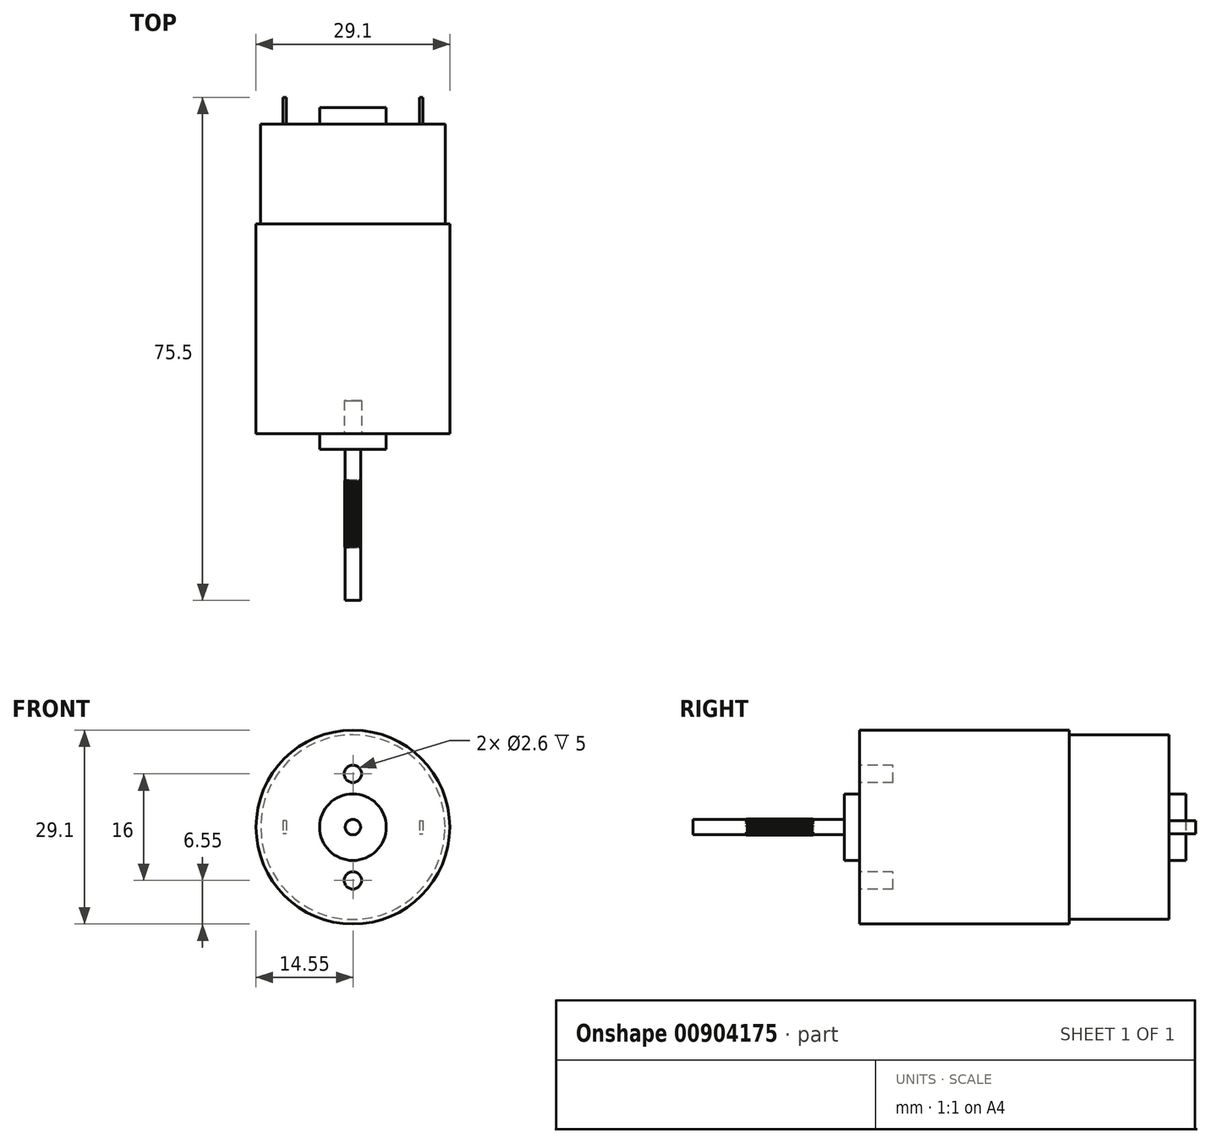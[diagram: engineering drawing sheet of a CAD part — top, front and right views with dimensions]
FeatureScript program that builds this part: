
annotation { "Feature Type Name" : "Feature", "Feature Type Description" : "" }
export const myFeature = defineFeature(function(context is Context, id is Id, definition is map)
    precondition{}
    {
        {
            var Q0;
            Q0=qCreatedBy(makeId("Front.planeOp"),FACE);
            var sketch = newSketch(context, id + "F0", { "sketchPlane" : qUnion([Q0])});
            skCircle(sketch, "E0", {"center": v(0, 0) * mm, "radius": 14.55 * mm});
            skSolve(sketch);
        }
        {
            var Q0;
            Q0 = qSketchRegion(id + "F0", true);
            extrude(context, id + "F1", {"entities" : qUnion([Q0]), "oppositeDirection" : true, "depth" : 31.5 * mm, "offsetDistance" : 25 * mm});
        }
        {
            var Q0;
            Q0=makeQuery(id+"F1.opExtrude","CAP_FACE",FACE,{"disambiguationData":[OSD([sQuery(id+"F0.wireOp",EDGE,"E0")])],"isStart":false});
            var sketch = newSketch(context, id + "F2", { "sketchPlane" : qUnion([Q0])});
            skCircle(sketch, "E1", {"center": v(0, 0) * mm, "radius": 13.85 * mm});
            skSolve(sketch);
        }
        {
            var Q0;
            Q0 = qSketchRegion(id + "F2", true);
            extrude(context, id + "F3", {"entities" : qUnion([Q0]), "operationType" : NewBodyOperationType.ADD, "depth" : 15 * mm, "offsetDistance" : 25 * mm});
        }
        {
            var Q0;
            Q0=makeQuery(id+"F1.opExtrude","CAP_FACE",FACE,{"disambiguationData":[OSD([sQuery(id+"F0.wireOp",EDGE,"E0")])],"isStart":true});
            var sketch = newSketch(context, id + "F4", { "sketchPlane" : qUnion([Q0])});
            skCircle(sketch, "E2", {"center": v(0, 0) * mm, "radius": 5 * mm});
            skSolve(sketch);
        }
        {
            var Q0;
            Q0 = qSketchRegion(id + "F4", true);
            extrude(context, id + "F5", {"entities" : qUnion([Q0]), "operationType" : NewBodyOperationType.ADD, "depth" : 2.3 * mm, "offsetDistance" : 25 * mm});
        }
        {
            var Q0;
            Q0=makeQuery(id+"F5.opExtrude","CAP_FACE",FACE,{"disambiguationData":[OSD([sQuery(id+"F4.wireOp",EDGE,"E2")])],"isStart":false});
            var sketch = newSketch(context, id + "F6", { "sketchPlane" : qUnion([Q0])});
            skCircle(sketch, "E3", {"center": v(0, 0) * mm, "radius": 1.15 * mm});
            skSolve(sketch);
        }
        {
            var Q0;
            Q0 = qSketchRegion(id + "F6", true);
            extrude(context, id + "F7", {"entities" : qUnion([Q0]), "operationType" : NewBodyOperationType.ADD, "depth" : 22.7 * mm, "offsetDistance" : 25 * mm});
        }
        {
            var Q0;
            Q0=makeQuery(id+"F1.opExtrude","CAP_FACE",FACE,{"disambiguationData":[OSD([sQuery(id+"F0.wireOp",EDGE,"E0")])],"isStart":true});
            var sketch = newSketch(context, id + "F8", { "sketchPlane" : qUnion([Q0])});
            skCircle(sketch, "E4", {"center": v(0, 8) * mm, "radius": 1.3 * mm});
            skCircle(sketch, "E5", {"center": v(0, -8) * mm, "radius": 1.3 * mm});
            skSolve(sketch);
        }
        {
            var Q0;
            Q0 = qSketchRegion(id + "F8", true);
            extrude(context, id + "F9", {"entities" : qUnion([Q0]), "operationType" : NewBodyOperationType.REMOVE, "oppositeDirection" : true, "depth" : 5 * mm, "offsetDistance" : 25 * mm});
        }
        {
            var Q0;
            Q0=makeQuery(id+"F3.opExtrude","CAP_FACE",FACE,{"disambiguationData":[OSD([sQuery(id+"F2.wireOp",EDGE,"E1")])],"isStart":false});
            var sketch = newSketch(context, id + "F10", { "sketchPlane" : qUnion([Q0])});
            skCircle(sketch, "E6", {"center": v(0, 0) * mm, "radius": 5 * mm});
            skSolve(sketch);
        }
        {
            var Q0;
            Q0 = qSketchRegion(id + "F10", true);
            extrude(context, id + "F11", {"entities" : qUnion([Q0]), "operationType" : NewBodyOperationType.ADD, "depth" : 2.5 * mm, "offsetDistance" : 25 * mm});
        }
        {
            var Q0;
            Q0=makeQuery(id+"F3.opExtrude","CAP_FACE",FACE,{"disambiguationData":[OSD([sQuery(id+"F2.wireOp",EDGE,"E1")])],"isStart":false});
            var sketch = newSketch(context, id + "F12", { "sketchPlane" : qUnion([Q0])});
            skLineSegment(sketch, "E7", {"start": v(-6.83, 0) * mm, "end": v(5.58, 0) * mm, "construction": true});
            skLineSegment(sketch, "E8", {"start": v(5.58, 0) * mm, "end": v(0, 4.4) * mm, "construction": true});
            skLineSegment(sketch, "E9", {"start": v(0, 4.4) * mm, "end": v(0, -3.18) * mm, "construction": true});
            skLineSegment(sketch, "E10.bottom", {"start": v(-10, 1) * mm, "end": v(-10.5, 1) * mm});
            skLineSegment(sketch, "E10.top", {"start": v(-10, -1) * mm, "end": v(-10.5, -1) * mm});
            skLineSegment(sketch, "E10.left", {"start": v(-10, 1) * mm, "end": v(-10, -1) * mm});
            skLineSegment(sketch, "E10.right", {"start": v(-10.5, 1) * mm, "end": v(-10.5, -1) * mm});
            skPoint(sketch, "E10.middle", {"position": v(-10.25, 0) * mm});
            skLineSegment(sketch, "E11.bottom", {"start": v(10, 1) * mm, "end": v(10.5, 1) * mm});
            skLineSegment(sketch, "E11.top", {"start": v(10, -1) * mm, "end": v(10.5, -1) * mm});
            skLineSegment(sketch, "E11.left", {"start": v(10, 1) * mm, "end": v(10, -1) * mm});
            skLineSegment(sketch, "E11.right", {"start": v(10.5, 1) * mm, "end": v(10.5, -1) * mm});
            skPoint(sketch, "E11.middle", {"position": v(10.25, 0) * mm});
            skSolve(sketch);
        }
        {
            var Q0;
            Q0 = qSketchRegion(id + "F12", true);
            extrude(context, id + "F13", {"entities" : qUnion([Q0]), "operationType" : NewBodyOperationType.ADD, "depth" : 4 * mm, "offsetDistance" : 25 * mm});
        }
        {
            var Q0;
            Q0=qCreatedBy(makeId("Front.planeOp"),FACE);
            cPlane(context, id + "F14", {"entities" : qUnion([Q0]), "cplaneType" : CPlaneType.OFFSET, "offset" : 7 * mm, "width" : 150 * mm, "height" : 150 * mm});
        }
        {
            var Q0;
            Q0=qCreatedBy(id+"F14.planeOp",FACE);
            var sketch = newSketch(context, id + "F15", { "sketchPlane" : qUnion([Q0])});
            skLineSegment(sketch, "E12", {"start": v(0, 0) * mm, "end": v(0.15, 0.99) * mm});
            skLineSegment(sketch, "E13", {"start": v(0.15, 0.99) * mm, "end": v(0, 1.2) * mm});
            skLineSegment(sketch, "E14", {"start": v(0, 1.2) * mm, "end": v(-0.15, 0.99) * mm});
            skLineSegment(sketch, "E15", {"start": v(-0.15, 0.99) * mm, "end": v(0, 0) * mm});
            skLineSegment(sketch, "E16.1.0", {"start": v(-0.2, 1.19) * mm, "end": v(-0.32, 0.95) * mm});
            skLineSegment(sketch, "E16.1.1", {"start": v(-0.02, 1) * mm, "end": v(-0.2, 1.19) * mm});
            skLineSegment(sketch, "E16.1.2", {"start": v(-0.32, 0.95) * mm, "end": v(0, 0) * mm});
            skLineSegment(sketch, "E16.1.3", {"start": v(0, 0) * mm, "end": v(-0.02, 1) * mm});
            skLineSegment(sketch, "E16.2.0", {"start": v(-0.41, 1.14) * mm, "end": v(-0.48, 0.89) * mm});
            skLineSegment(sketch, "E16.2.1", {"start": v(-0.2, 1) * mm, "end": v(-0.41, 1.14) * mm});
            skLineSegment(sketch, "E16.2.2", {"start": v(-0.48, 0.89) * mm, "end": v(0, 0.01) * mm});
            skLineSegment(sketch, "E16.2.3", {"start": v(0, 0.01) * mm, "end": v(-0.2, 1) * mm});
            skLineSegment(sketch, "E16.3.0", {"start": v(-0.6, 1.06) * mm, "end": v(-0.63, 0.8) * mm});
            skLineSegment(sketch, "E16.3.1", {"start": v(-0.37, 0.95) * mm, "end": v(-0.6, 1.06) * mm});
            skLineSegment(sketch, "E16.3.2", {"start": v(-0.63, 0.8) * mm, "end": v(0, 0.02) * mm});
            skLineSegment(sketch, "E16.3.3", {"start": v(0, 0.02) * mm, "end": v(-0.37, 0.95) * mm});
            skLineSegment(sketch, "E16.4.0", {"start": v(-0.78, 0.94) * mm, "end": v(-0.75, 0.68) * mm});
            skLineSegment(sketch, "E16.4.1", {"start": v(-0.52, 0.88) * mm, "end": v(-0.78, 0.94) * mm});
            skLineSegment(sketch, "E16.4.2", {"start": v(-0.75, 0.68) * mm, "end": v(0, 0.02) * mm});
            skLineSegment(sketch, "E16.4.3", {"start": v(0, 0.02) * mm, "end": v(-0.52, 0.88) * mm});
            skLineSegment(sketch, "E16.5.0", {"start": v(-0.93, 0.8) * mm, "end": v(-0.86, 0.55) * mm});
            skLineSegment(sketch, "E16.5.1", {"start": v(-0.67, 0.78) * mm, "end": v(-0.93, 0.8) * mm});
            skLineSegment(sketch, "E16.5.2", {"start": v(-0.86, 0.55) * mm, "end": v(0, 0.03) * mm});
            skLineSegment(sketch, "E16.5.3", {"start": v(0, 0.03) * mm, "end": v(-0.67, 0.78) * mm});
            skLineSegment(sketch, "E16.6.0", {"start": v(-1.05, 0.63) * mm, "end": v(-0.94, 0.4) * mm});
            skLineSegment(sketch, "E16.6.1", {"start": v(-0.8, 0.65) * mm, "end": v(-1.05, 0.63) * mm});
            skLineSegment(sketch, "E16.6.2", {"start": v(-0.94, 0.4) * mm, "end": v(-0.01, 0.03) * mm});
            skLineSegment(sketch, "E16.6.3", {"start": v(-0.01, 0.03) * mm, "end": v(-0.8, 0.65) * mm});
            skLineSegment(sketch, "E16.7.0", {"start": v(-1.14, 0.44) * mm, "end": v(-1, 0.23) * mm});
            skLineSegment(sketch, "E16.7.1", {"start": v(-0.9, 0.51) * mm, "end": v(-1.14, 0.44) * mm});
            skLineSegment(sketch, "E16.7.2", {"start": v(-1, 0.23) * mm, "end": v(-0.02, 0.03) * mm});
            skLineSegment(sketch, "E16.7.3", {"start": v(-0.02, 0.03) * mm, "end": v(-0.9, 0.51) * mm});
            skLineSegment(sketch, "E16.8.0", {"start": v(-1.2, 0.24) * mm, "end": v(-1.02, 0.06) * mm});
            skLineSegment(sketch, "E16.8.1", {"start": v(-0.97, 0.35) * mm, "end": v(-1.2, 0.24) * mm});
            skLineSegment(sketch, "E16.8.2", {"start": v(-1.02, 0.06) * mm, "end": v(-0.02, 0.04) * mm});
            skLineSegment(sketch, "E16.8.3", {"start": v(-0.02, 0.04) * mm, "end": v(-0.97, 0.35) * mm});
            skLineSegment(sketch, "E16.9.0", {"start": v(-1.23, 0.04) * mm, "end": v(-1.01, -0.11) * mm});
            skLineSegment(sketch, "E16.9.1", {"start": v(-1.01, 0.19) * mm, "end": v(-1.23, 0.04) * mm});
            skLineSegment(sketch, "E16.9.2", {"start": v(-1.01, -0.11) * mm, "end": v(-0.03, 0.04) * mm});
            skLineSegment(sketch, "E16.9.3", {"start": v(-0.03, 0.04) * mm, "end": v(-1.01, 0.19) * mm});
            skLineSegment(sketch, "E16.10.0", {"start": v(-1.21, -0.17) * mm, "end": v(-0.98, -0.28) * mm});
            skLineSegment(sketch, "E16.10.1", {"start": v(-1.03, 0.01) * mm, "end": v(-1.21, -0.17) * mm});
            skLineSegment(sketch, "E16.10.2", {"start": v(-0.98, -0.28) * mm, "end": v(-0.03, 0.04) * mm});
            skLineSegment(sketch, "E16.10.3", {"start": v(-0.03, 0.04) * mm, "end": v(-1.03, 0.01) * mm});
            skLineSegment(sketch, "E16.11.0", {"start": v(-1.16, -0.37) * mm, "end": v(-0.91, -0.44) * mm});
            skLineSegment(sketch, "E16.11.1", {"start": v(-1.02, -0.16) * mm, "end": v(-1.16, -0.37) * mm});
            skLineSegment(sketch, "E16.11.2", {"start": v(-0.91, -0.44) * mm, "end": v(-0.04, 0.04) * mm});
            skLineSegment(sketch, "E16.11.3", {"start": v(-0.04, 0.04) * mm, "end": v(-1.02, -0.16) * mm});
            skLineSegment(sketch, "E16.12.0", {"start": v(-1.08, -0.56) * mm, "end": v(-0.82, -0.59) * mm});
            skLineSegment(sketch, "E16.12.1", {"start": v(-0.97, -0.33) * mm, "end": v(-1.08, -0.56) * mm});
            skLineSegment(sketch, "E16.12.2", {"start": v(-0.82, -0.59) * mm, "end": v(-0.04, 0.04) * mm});
            skLineSegment(sketch, "E16.12.3", {"start": v(-0.04, 0.04) * mm, "end": v(-0.97, -0.33) * mm});
            skLineSegment(sketch, "E16.13.0", {"start": v(-0.97, -0.74) * mm, "end": v(-0.7, -0.72) * mm});
            skLineSegment(sketch, "E16.13.1", {"start": v(-0.9, -0.49) * mm, "end": v(-0.97, -0.74) * mm});
            skLineSegment(sketch, "E16.13.2", {"start": v(-0.7, -0.72) * mm, "end": v(-0.05, 0.03) * mm});
            skLineSegment(sketch, "E16.13.3", {"start": v(-0.05, 0.03) * mm, "end": v(-0.9, -0.49) * mm});
            skLineSegment(sketch, "E16.14.0", {"start": v(-0.82, -0.89) * mm, "end": v(-0.57, -0.82) * mm});
            skLineSegment(sketch, "E16.14.1", {"start": v(-0.8, -0.63) * mm, "end": v(-0.82, -0.89) * mm});
            skLineSegment(sketch, "E16.14.2", {"start": v(-0.57, -0.82) * mm, "end": v(-0.05, 0.03) * mm});
            skLineSegment(sketch, "E16.14.3", {"start": v(-0.05, 0.03) * mm, "end": v(-0.8, -0.63) * mm});
            skLineSegment(sketch, "E16.15.0", {"start": v(-0.66, -1.01) * mm, "end": v(-0.42, -0.9) * mm});
            skLineSegment(sketch, "E16.15.1", {"start": v(-0.68, -0.76) * mm, "end": v(-0.66, -1.01) * mm});
            skLineSegment(sketch, "E16.15.2", {"start": v(-0.42, -0.9) * mm, "end": v(-0.06, 0.03) * mm});
            skLineSegment(sketch, "E16.15.3", {"start": v(-0.06, 0.03) * mm, "end": v(-0.68, -0.76) * mm});
            skLineSegment(sketch, "E16.16.0", {"start": v(-0.47, -1.1) * mm, "end": v(-0.26, -0.96) * mm});
            skLineSegment(sketch, "E16.16.1", {"start": v(-0.54, -0.86) * mm, "end": v(-0.47, -1.1) * mm});
            skLineSegment(sketch, "E16.16.2", {"start": v(-0.26, -0.96) * mm, "end": v(-0.06, 0.02) * mm});
            skLineSegment(sketch, "E16.16.3", {"start": v(-0.06, 0.02) * mm, "end": v(-0.54, -0.86) * mm});
            skLineSegment(sketch, "E16.17.0", {"start": v(-0.27, -1.17) * mm, "end": v(-0.09, -0.98) * mm});
            skLineSegment(sketch, "E16.17.1", {"start": v(-0.38, -0.93) * mm, "end": v(-0.27, -1.17) * mm});
            skLineSegment(sketch, "E16.17.2", {"start": v(-0.09, -0.98) * mm, "end": v(-0.06, 0.02) * mm});
            skLineSegment(sketch, "E16.17.3", {"start": v(-0.06, 0.02) * mm, "end": v(-0.38, -0.93) * mm});
            skLineSegment(sketch, "E16.18.0", {"start": v(-0.06, -1.19) * mm, "end": v(0.09, -0.98) * mm});
            skLineSegment(sketch, "E16.18.1", {"start": v(-0.21, -0.98) * mm, "end": v(-0.06, -1.19) * mm});
            skLineSegment(sketch, "E16.18.2", {"start": v(0.09, -0.98) * mm, "end": v(-0.06, 0.01) * mm});
            skLineSegment(sketch, "E16.18.3", {"start": v(-0.06, 0.01) * mm, "end": v(-0.21, -0.98) * mm});
            skLineSegment(sketch, "E16.19.0", {"start": v(0.14, -1.18) * mm, "end": v(0.26, -0.94) * mm});
            skLineSegment(sketch, "E16.19.1", {"start": v(-0.04, -1) * mm, "end": v(0.14, -1.18) * mm});
            skLineSegment(sketch, "E16.19.2", {"start": v(0.26, -0.94) * mm, "end": v(-0.06, 0) * mm});
            skLineSegment(sketch, "E16.19.3", {"start": v(-0.06, 0) * mm, "end": v(-0.04, -1) * mm});
            skLineSegment(sketch, "E16.20.0", {"start": v(0.35, -1.13) * mm, "end": v(0.42, -0.88) * mm});
            skLineSegment(sketch, "E16.20.1", {"start": v(0.13, -0.98) * mm, "end": v(0.35, -1.13) * mm});
            skLineSegment(sketch, "E16.20.2", {"start": v(0.42, -0.88) * mm, "end": v(-0.06, 0) * mm});
            skLineSegment(sketch, "E16.20.3", {"start": v(-0.06, 0) * mm, "end": v(0.13, -0.98) * mm});
            skLineSegment(sketch, "E16.21.0", {"start": v(0.54, -1.05) * mm, "end": v(0.56, -0.79) * mm});
            skLineSegment(sketch, "E16.21.1", {"start": v(0.3, -0.94) * mm, "end": v(0.54, -1.05) * mm});
            skLineSegment(sketch, "E16.21.2", {"start": v(0.56, -0.79) * mm, "end": v(-0.06, 0) * mm});
            skLineSegment(sketch, "E16.21.3", {"start": v(-0.06, 0) * mm, "end": v(0.3, -0.94) * mm});
            skLineSegment(sketch, "E16.22.0", {"start": v(0.71, -0.93) * mm, "end": v(0.7, -0.67) * mm});
            skLineSegment(sketch, "E16.22.1", {"start": v(0.46, -0.86) * mm, "end": v(0.71, -0.93) * mm});
            skLineSegment(sketch, "E16.22.2", {"start": v(0.7, -0.67) * mm, "end": v(-0.06, -0.01) * mm});
            skLineSegment(sketch, "E16.22.3", {"start": v(-0.06, -0.01) * mm, "end": v(0.46, -0.86) * mm});
            skLineSegment(sketch, "E16.23.0", {"start": v(0.86, -0.79) * mm, "end": v(0.8, -0.54) * mm});
            skLineSegment(sketch, "E16.23.1", {"start": v(0.6, -0.77) * mm, "end": v(0.86, -0.79) * mm});
            skLineSegment(sketch, "E16.23.2", {"start": v(0.8, -0.54) * mm, "end": v(-0.06, -0.02) * mm});
            skLineSegment(sketch, "E16.23.3", {"start": v(-0.06, -0.02) * mm, "end": v(0.6, -0.77) * mm});
            skLineSegment(sketch, "E16.24.0", {"start": v(0.99, -0.62) * mm, "end": v(0.88, -0.38) * mm});
            skLineSegment(sketch, "E16.24.1", {"start": v(0.73, -0.64) * mm, "end": v(0.99, -0.62) * mm});
            skLineSegment(sketch, "E16.24.2", {"start": v(0.88, -0.38) * mm, "end": v(-0.05, -0.02) * mm});
            skLineSegment(sketch, "E16.24.3", {"start": v(-0.05, -0.02) * mm, "end": v(0.73, -0.64) * mm});
            skLineSegment(sketch, "E16.25.0", {"start": v(1.08, -0.43) * mm, "end": v(0.93, -0.22) * mm});
            skLineSegment(sketch, "E16.25.1", {"start": v(0.83, -0.5) * mm, "end": v(1.08, -0.43) * mm});
            skLineSegment(sketch, "E16.25.2", {"start": v(0.93, -0.22) * mm, "end": v(-0.05, -0.02) * mm});
            skLineSegment(sketch, "E16.25.3", {"start": v(-0.05, -0.02) * mm, "end": v(0.83, -0.5) * mm});
            skLineSegment(sketch, "E16.26.0", {"start": v(1.14, -0.23) * mm, "end": v(0.96, -0.05) * mm});
            skLineSegment(sketch, "E16.26.1", {"start": v(0.9, -0.34) * mm, "end": v(1.14, -0.23) * mm});
            skLineSegment(sketch, "E16.26.2", {"start": v(0.96, -0.05) * mm, "end": v(-0.04, -0.02) * mm});
            skLineSegment(sketch, "E16.26.3", {"start": v(-0.04, -0.02) * mm, "end": v(0.9, -0.34) * mm});
            skLineSegment(sketch, "E16.27.0", {"start": v(1.16, -0.03) * mm, "end": v(0.95, 0.12) * mm});
            skLineSegment(sketch, "E16.27.1", {"start": v(0.95, -0.18) * mm, "end": v(1.16, -0.03) * mm});
            skLineSegment(sketch, "E16.27.2", {"start": v(0.95, 0.12) * mm, "end": v(-0.04, -0.03) * mm});
            skLineSegment(sketch, "E16.27.3", {"start": v(-0.04, -0.03) * mm, "end": v(0.95, -0.18) * mm});
            skLineSegment(sketch, "E16.28.0", {"start": v(1.15, 0.18) * mm, "end": v(0.92, 0.3) * mm});
            skLineSegment(sketch, "E16.28.1", {"start": v(0.97, 0) * mm, "end": v(1.15, 0.18) * mm});
            skLineSegment(sketch, "E16.28.2", {"start": v(0.92, 0.3) * mm, "end": v(-0.03, -0.03) * mm});
            skLineSegment(sketch, "E16.28.3", {"start": v(-0.03, -0.03) * mm, "end": v(0.97, 0) * mm});
            skLineSegment(sketch, "E16.29.0", {"start": v(1.1, 0.38) * mm, "end": v(0.85, 0.45) * mm});
            skLineSegment(sketch, "E16.29.1", {"start": v(0.95, 0.17) * mm, "end": v(1.1, 0.38) * mm});
            skLineSegment(sketch, "E16.29.2", {"start": v(0.85, 0.45) * mm, "end": v(-0.03, -0.03) * mm});
            skLineSegment(sketch, "E16.29.3", {"start": v(-0.03, -0.03) * mm, "end": v(0.95, 0.17) * mm});
            skLineSegment(sketch, "E16.30.0", {"start": v(1.02, 0.58) * mm, "end": v(0.76, 0.6) * mm});
            skLineSegment(sketch, "E16.30.1", {"start": v(0.91, 0.34) * mm, "end": v(1.02, 0.58) * mm});
            skLineSegment(sketch, "E16.30.2", {"start": v(0.76, 0.6) * mm, "end": v(-0.02, -0.02) * mm});
            skLineSegment(sketch, "E16.30.3", {"start": v(-0.02, -0.02) * mm, "end": v(0.91, 0.34) * mm});
            skLineSegment(sketch, "E16.31.0", {"start": v(0.9, 0.75) * mm, "end": v(0.65, 0.73) * mm});
            skLineSegment(sketch, "E16.31.1", {"start": v(0.84, 0.5) * mm, "end": v(0.9, 0.75) * mm});
            skLineSegment(sketch, "E16.31.2", {"start": v(0.65, 0.73) * mm, "end": v(-0.02, -0.02) * mm});
            skLineSegment(sketch, "E16.31.3", {"start": v(-0.02, -0.02) * mm, "end": v(0.84, 0.5) * mm});
            skLineSegment(sketch, "E16.32.0", {"start": v(0.76, 0.9) * mm, "end": v(0.5, 0.83) * mm});
            skLineSegment(sketch, "E16.32.1", {"start": v(0.74, 0.64) * mm, "end": v(0.76, 0.9) * mm});
            skLineSegment(sketch, "E16.32.2", {"start": v(0.5, 0.83) * mm, "end": v(-0.01, -0.02) * mm});
            skLineSegment(sketch, "E16.32.3", {"start": v(-0.01, -0.02) * mm, "end": v(0.74, 0.64) * mm});
            skLineSegment(sketch, "E16.33.0", {"start": v(0.6, 1.02) * mm, "end": v(0.36, 0.92) * mm});
            skLineSegment(sketch, "E16.33.1", {"start": v(0.62, 0.77) * mm, "end": v(0.6, 1.02) * mm});
            skLineSegment(sketch, "E16.33.2", {"start": v(0.36, 0.92) * mm, "end": v(0, -0.02) * mm});
            skLineSegment(sketch, "E16.33.3", {"start": v(0, -0.02) * mm, "end": v(0.62, 0.77) * mm});
            skLineSegment(sketch, "E16.34.0", {"start": v(0.4, 1.12) * mm, "end": v(0.2, 0.97) * mm});
            skLineSegment(sketch, "E16.34.1", {"start": v(0.48, 0.87) * mm, "end": v(0.4, 1.12) * mm});
            skLineSegment(sketch, "E16.34.2", {"start": v(0.2, 0.97) * mm, "end": v(0, -0.01) * mm});
            skLineSegment(sketch, "E16.34.3", {"start": v(0, -0.01) * mm, "end": v(0.48, 0.87) * mm});
            skLineSegment(sketch, "E16.35.0", {"start": v(0.2, 1.18) * mm, "end": v(0.02, 1) * mm});
            skLineSegment(sketch, "E16.35.1", {"start": v(0.32, 0.94) * mm, "end": v(0.2, 1.18) * mm});
            skLineSegment(sketch, "E16.35.2", {"start": v(0.02, 1) * mm, "end": v(0, 0) * mm});
            skLineSegment(sketch, "E16.35.3", {"start": v(0, 0) * mm, "end": v(0.32, 0.94) * mm});
            skPoint(sketch, "E16.center", {"position": v(-0.03, 0) * mm});
            skSolve(sketch);
        }
        {
            var Q0;
            Q0 = qSketchRegion(id + "F15", true);
            extrude(context, id + "F16", {"entities" : qUnion([Q0]), "operationType" : NewBodyOperationType.ADD, "depth" : 10 * mm, "offsetDistance" : 25 * mm});
        }
    });
